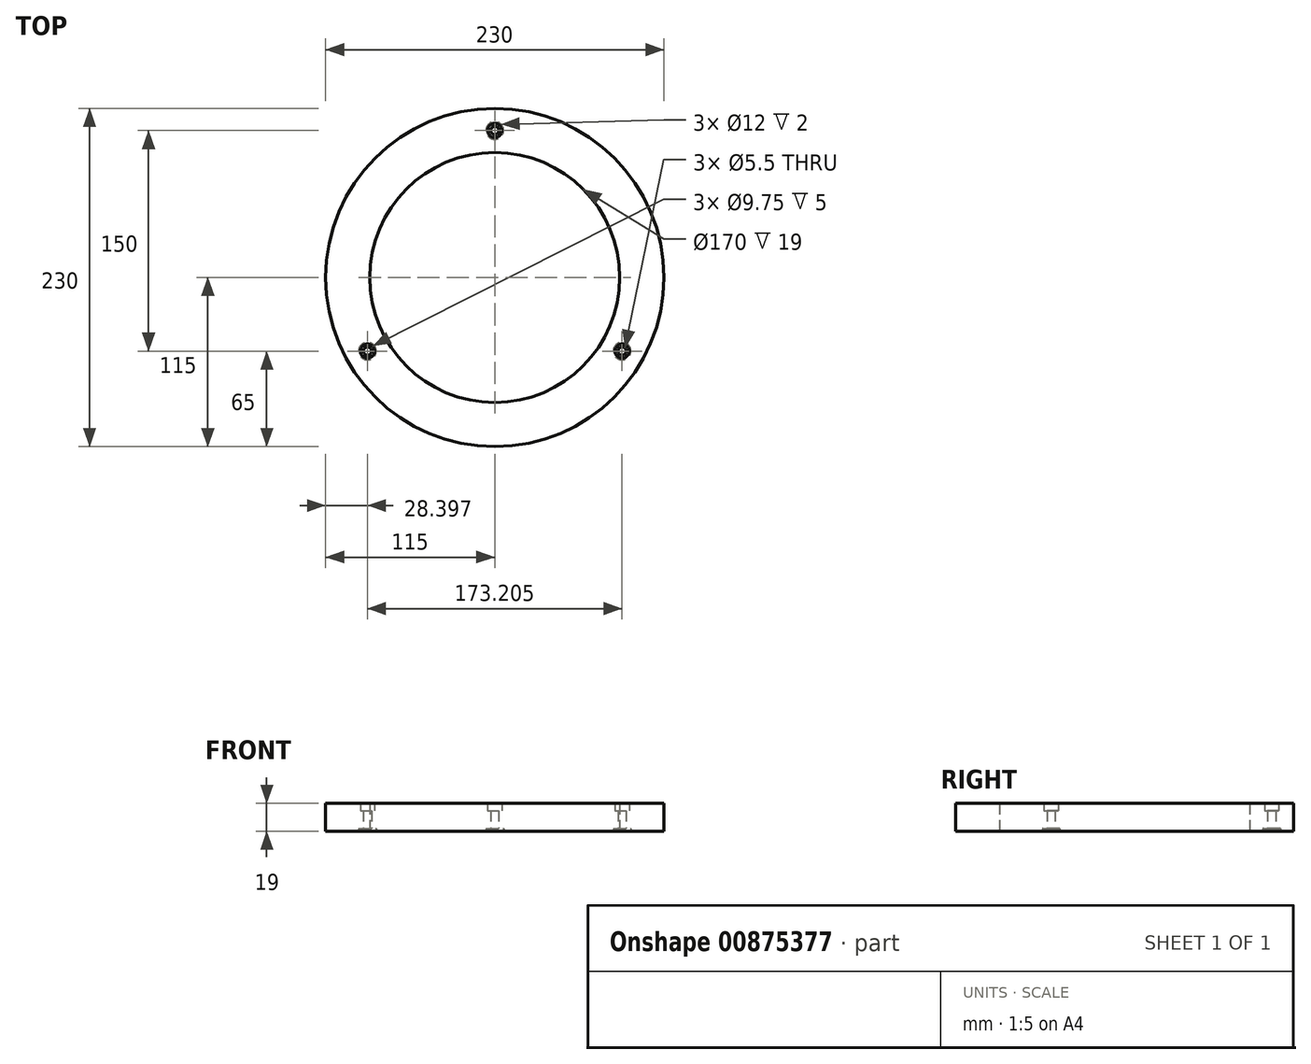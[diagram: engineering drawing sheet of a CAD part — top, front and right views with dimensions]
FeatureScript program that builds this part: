
annotation { "Feature Type Name" : "Feature", "Feature Type Description" : "" }
export const myFeature = defineFeature(function(context is Context, id is Id, definition is map)
    precondition{}
    {
        {
            var Q0;
            Q0=qCreatedBy(makeId("Top.planeOp"),FACE);
            var sketch = newSketch(context, id + "F0", { "sketchPlane" : qUnion([Q0])});
            skCircle(sketch, "E0", {"center": v(0, 0) * mm, "radius": 85 * mm});
            skCircle(sketch, "E1.0", {"center": v(0, 0) * mm, "radius": 115 * mm});
            skSolve(sketch);
        }
        {
            var Q0;
            Q0=makeQuery(id+"F0.imprint","IMPRINT",FACE,{"disambiguationData":[TD([[makeQuery(id+"F0.imprint","IMPRINT",EDGE,{"derivedFrom":sQuery(id+"F0.wireOp",EDGE,"E0")}),-1.0]])]});
            extrude(context, id + "F1", {"entities" : qUnion([Q0]), "depth" : 19 * mm, "offsetDistance" : 25 * mm});
        }
        {
            var Q0;
            Q0=makeQuery(id+"F1.opExtrude","CAP_FACE",FACE,{"disambiguationData":[OSD([sQuery(id+"F0.wireOp",EDGE,"E0"),sQuery(id+"F0.wireOp",EDGE,"E1.0")])],"isStart":true});
            var sketch = newSketch(context, id + "F2", { "sketchPlane" : qUnion([Q0])});
            skPoint(sketch, "E2.center", {"position": v(0, 0) * mm});
            skLineSegment(sketch, "E3", {"start": v(0, -85) * mm, "end": v(0, -115) * mm, "construction": true});
            skCircle(sketch, "E4", {"center": v(0, -100) * mm, "radius": 6 * mm});
            skCircle(sketch, "E5.1.0", {"center": v(86.6, 50) * mm, "radius": 6 * mm});
            skCircle(sketch, "E5.2.0", {"center": v(-86.6, 50) * mm, "radius": 6 * mm});
            skSolve(sketch);
        }
        {
            var Q0;
            Q0 = qSketchRegion(id + "F2", true);
            extrude(context, id + "F3", {"entities" : qUnion([Q0]), "operationType" : NewBodyOperationType.REMOVE, "oppositeDirection" : true, "depth" : 2 * mm, "offsetDistance" : 25 * mm});
        }
        {
            var Q0;
            Q0=makeQuery(id+"F1.opExtrude","CAP_FACE",FACE,{"disambiguationData":[OSD([sQuery(id+"F0.wireOp",EDGE,"E0"),sQuery(id+"F0.wireOp",EDGE,"E1.0")])],"isStart":false});
            var sketch = newSketch(context, id + "F4", { "sketchPlane" : qUnion([Q0])});
            skLineSegment(sketch, "E6", {"start": v(0, 115) * mm, "end": v(0, 85) * mm, "construction": true});
            skPoint(sketch, "E7", {"position": v(0, 100) * mm});
            skPoint(sketch, "E8.1.0", {"position": v(-86.6, -50) * mm});
            skPoint(sketch, "E8.2.0", {"position": v(86.6, -50) * mm});
            skPoint(sketch, "E8.center", {"position": v(0, 0) * mm});
            skSolve(sketch);
        }
        {
            var Q0;
            Q0=sQuery(id+"F4.wireOp",VERTEX,"E7");
            var Q1;
            Q1=sQuery(id+"F4.wireOp",VERTEX,"E8.2.0");
            var Q2;
            Q2=sQuery(id+"F4.wireOp",VERTEX,"E8.1.0");
            var Q3;
            Q3=makeQuery(id+"F1.opExtrude","SWEPT_BODY",BODY,{"disambiguationData":[OSD([sQuery(id+"F0.wireOp",EDGE,"E0"),sQuery(id+"F0.wireOp",EDGE,"E1.0")])]});
            hole(context, id + "F5", {"style" : HoleStyle.C_BORE, "endStyle" : HoleEndStyle.THROUGH, "standardTappedOrClearance" : lookupTablePath({ "fit" : "Normal", "standard" : "ISO", "size" : "M5", "type" : "Clearance" }), "standardBlindInLast" : lookupTablePath({ "fit" : "Normal", "standard" : "ISO", "size" : "M5", "type" : "Clearance" }), "holeDiameter" : 5.5 * mm, "cBoreDiameter" : 9.75 * mm, "cBoreDepth" : 5 * mm, "majorDiameter" : 5 * mm, "isTappedThrough" : true, "tappedDepth" : 15 * mm, "tapClearance" : 3, "locations" : qUnion([Q0, Q1, Q2]), "scope" : qUnion([Q3]), "startStyle" : HoleStartStyle.SKETCH});
        }
    });
